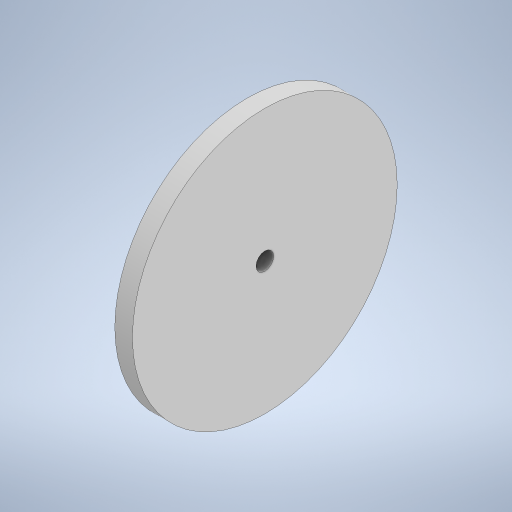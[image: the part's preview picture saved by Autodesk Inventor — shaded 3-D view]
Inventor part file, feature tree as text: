
AUTODESK INVENTOR PART (.ipt)
format: ipt  version: 2023.2 (Build 272271000, 271)  size: 247,808 bytes
history: native  units: mm
features: sketch x1
ambient origin geometry x8: Origin, YZ Plane, XZ Plane, XY Plane, X Axis, Y Axis, Z Axis, Center Point
bodies: Body1 (feature_tree)
feature tree (1):
  sketch  "Sketch1"  dims[d228=60.0mm d229=4.0mm d230=0.0mm d231=4.0mm d232=6.0mm d233=4.0mm d234=2.0mm d235=90.0deg d236=8.0mm d237=20.594885mm d9=0.5mm d10=0.872665mm d11=0.5mm d12=0.872665mm d13=0.5mm d14=0.872665mm d27=0.5mm d28=0.872665mm d29=0.5mm d30=0.872665mm d88=0.5mm d89=0.872665mm d90=0.5mm d91=0.872665mm d116=0.5mm d117=0.872665mm d118=0.5mm d119=0.872665mm d154=0.5mm d155=0.872665mm d156=0.5mm d157=0.872665mm d181=0.5mm d182=0.872665mm d183=0.5mm d184=0.872665mm d221=0.5mm d222=0.872665mm d223=0.5mm d224=0.872665mm]
